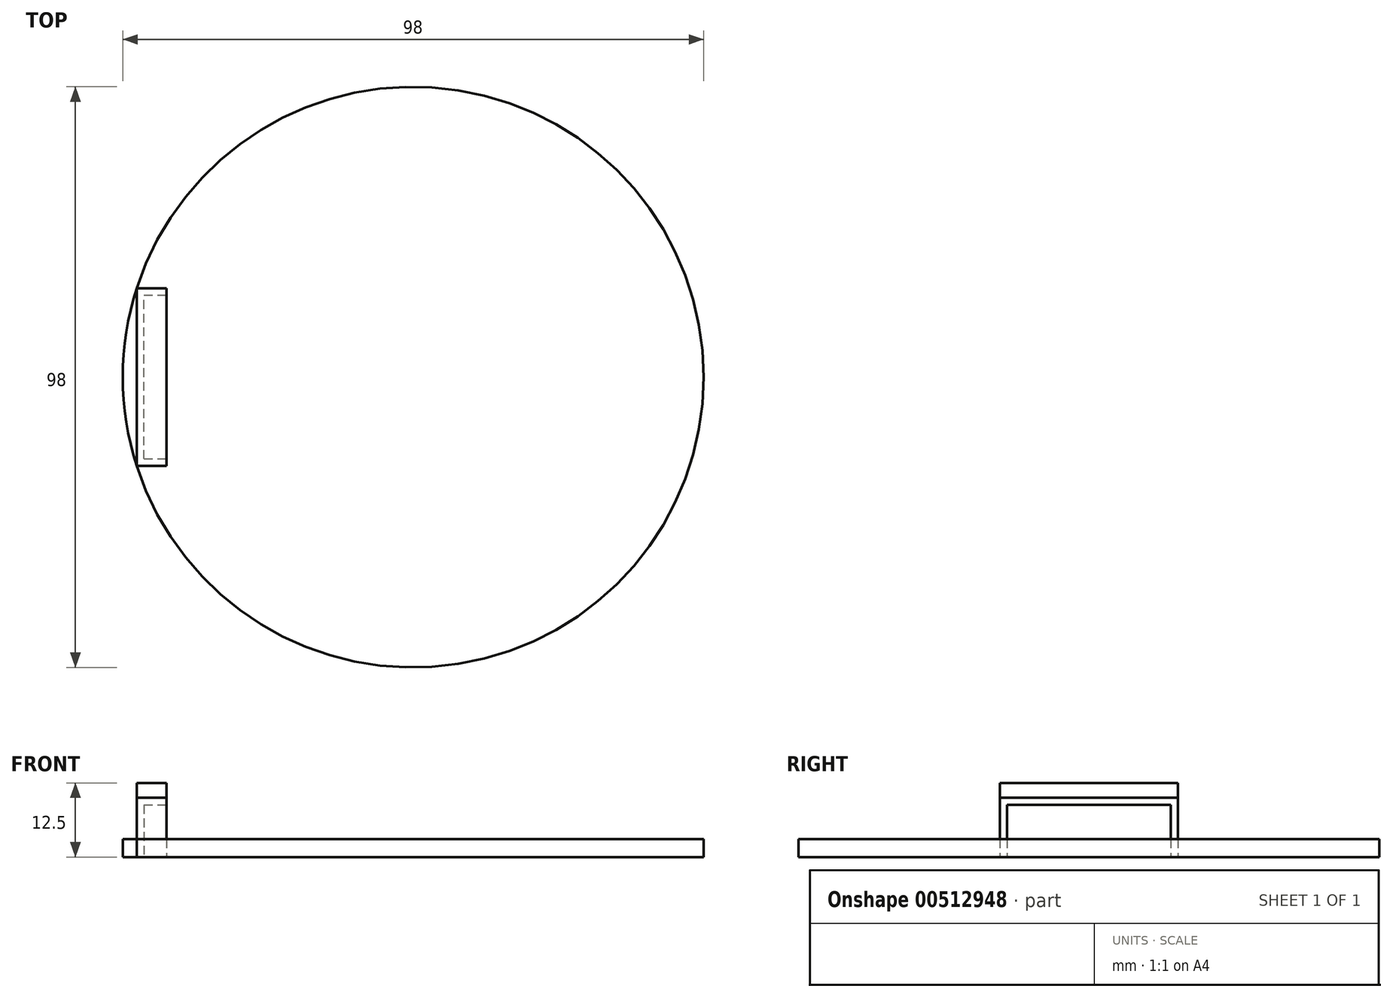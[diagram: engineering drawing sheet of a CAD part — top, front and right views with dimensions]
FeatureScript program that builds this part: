
annotation { "Feature Type Name" : "Feature", "Feature Type Description" : "" }
export const myFeature = defineFeature(function(context is Context, id is Id, definition is map)
    precondition{}
    {
        {
            var Q0;
            Q0=qCreatedBy(makeId("Top.planeOp"),FACE);
            var sketch = newSketch(context, id + "F0", { "sketchPlane" : qUnion([Q0])});
            skLineSegment(sketch, "E0", {"start": v(0, 0) * mm, "end": v(-49, 0) * mm});
            skArc(sketch, "E1", {"start": v(0, 49) * mm, "mid": v(-49, 0) * mm, "end": v(0, -49) * mm});
            skLineSegment(sketch, "E2", {"start": v(-46.65, -15) * mm, "end": v(-46.65, 15) * mm});
            skLineSegment(sketch, "E3", {"start": v(-46.65, -15) * mm, "end": v(-41.65, -15) * mm});
            skLineSegment(sketch, "E4", {"start": v(-41.65, -15) * mm, "end": v(-41.65, 15) * mm});
            skLineSegment(sketch, "E5", {"start": v(-41.65, 15) * mm, "end": v(-46.65, 15) * mm});
            skArc(sketch, "E6", {"start": v(0, -49) * mm, "mid": v(49, 0) * mm, "end": v(0, 49) * mm});
            skSolve(sketch);
        }
        {
            var Q0;
            {var subQ1=sQuery(id+"F0.wireOp",EDGE,"E3");Q0=makeQuery(id+"F0.imprint","IMPRINT",FACE,{"disambiguationData":[TD([[makeQuery(id+"F0.imprint","IMPRINT",EDGE,{"derivedFrom":subQ1}),-1.0]])]});}
            var Q1;
            {var subQ0=sQuery(id+"F0.wireOp",EDGE,"E1");var subQ1=sQuery(id+"F0.wireOp",EDGE,"E0");var subQ2=makeQuery(id+"F0.imprint","INTERSECT",VERTEX,{"derivedFrom":[subQ1,subQ0]});Q1=makeQuery(id+"F0.imprint","IMPRINT",FACE,{"disambiguationData":[TD([[makeQuery(id+"F0.imprint","IMPRINT",EDGE,{"disambiguationData":[TD([[subQ2,1.0]])],"derivedFrom":subQ1}),1.0]])]});}
            var Q2;
            {var subQ0=sQuery(id+"F0.wireOp",EDGE,"E1");var subQ1=sQuery(id+"F0.wireOp",EDGE,"E0");var subQ2=makeQuery(id+"F0.imprint","INTERSECT",VERTEX,{"derivedFrom":[subQ1,subQ0]});Q2=makeQuery(id+"F0.imprint","IMPRINT",FACE,{"disambiguationData":[TD([[makeQuery(id+"F0.imprint","IMPRINT",EDGE,{"disambiguationData":[TD([[subQ2,1.0]])],"derivedFrom":subQ1}),-1.0]])]});}
            extrude(context, id + "F1", {"entities" : qUnion([Q0, Q1, Q2]), "oppositeDirection" : true, "depth" : 3 * mm, "offsetDistance" : 25 * mm});
        }
        {
            var Q0;
            {var subQ5=sQuery(id+"F0.wireOp",EDGE,"E3");Q0=makeQuery(id+"F0.imprint","IMPRINT",FACE,{"disambiguationData":[TD([[makeQuery(id+"F0.imprint","IMPRINT",EDGE,{"derivedFrom":subQ5}),1.0]])]});}
            var Q1;
            {var subQ5=sQuery(id+"F0.wireOp",EDGE,"E5");Q1=makeQuery(id+"F0.imprint","IMPRINT",FACE,{"disambiguationData":[TD([[makeQuery(id+"F0.imprint","IMPRINT",EDGE,{"derivedFrom":subQ5}),1.0]])]});}
            var Q2;
            Q2=sQuery(id+"F0.wireOp",EDGE,"E3");
            var Q3;
            Q3=sQuery(id+"F0.wireOp",EDGE,"E2");
            var Q4;
            Q4=sQuery(id+"F0.wireOp",EDGE,"E5");
            extrude(context, id + "F2", {"entities" : qUnion([Q0, Q1]), "surfaceEntities" : qUnion([Q2, Q3, Q4]), "oppositeDirection" : true, "depth" : 10 * mm, "offsetDistance" : 25 * mm});
        }
        {
            var Q0;
            Q0=qCreatedBy(makeId("Top.planeOp"),FACE);
            cPlane(context, id + "F3", {"entities" : qUnion([Q0]), "cplaneType" : CPlaneType.OFFSET, "offset" : 10 * mm, "oppositeDirection" : true, "width" : 150 * mm, "height" : 150 * mm});
        }
        {
            var Q0;
            Q0=qCreatedBy(id+"F3.planeOp",FACE);
            var sketch = newSketch(context, id + "F4", { "sketchPlane" : qUnion([Q0])});
            skPoint(sketch, "E7.0", {"position": v(-41.65, 15) * mm});
            skPoint(sketch, "E8.0", {"position": v(-46.65, 15) * mm});
            skPoint(sketch, "E9.0", {"position": v(-46.65, -15) * mm});
            skPoint(sketch, "E10.0", {"position": v(-41.65, -15) * mm});
            skLineSegment(sketch, "E11", {"start": v(-46.65, 15) * mm, "end": v(-46.65, -15) * mm});
            skLineSegment(sketch, "E12", {"start": v(-41.65, -15) * mm, "end": v(-46.65, -15) * mm});
            skLineSegment(sketch, "E13", {"start": v(-46.65, 15) * mm, "end": v(-41.65, 15) * mm});
            skLineSegment(sketch, "E14", {"start": v(-41.65, 15) * mm, "end": v(-41.65, -15) * mm});
            skSolve(sketch);
        }
        {
            var Q0;
            Q0=qSketchRegion(id+"F4",true);
            var Q1;
            Q1=qConstructionFilter(qBodyType(qCreatedBy(id+"F4",EDGE),BodyType.WIRE),ConstructionObject.NO);
            extrude(context, id + "F5", {"entities" : qUnion([Q0]), "surfaceEntities" : qUnion([Q1]), "oppositeDirection" : true, "depth" : 2.5 * mm, "offsetDistance" : 25 * mm});
        }
        {
            var Q0;
            Q0=makeQuery(id+"F1.opExtrude","SWEPT_BODY",BODY,{"disambiguationData":[OSD([sQuery(id+"F0.wireOp",EDGE,"E1"),sQuery(id+"F0.wireOp",EDGE,"E3"),sQuery(id+"F0.wireOp",EDGE,"E4"),sQuery(id+"F0.wireOp",EDGE,"E5"),sQuery(id+"F0.wireOp",EDGE,"E6")])]});
            var Q1;
            Q1=makeQuery(id+"F1.opExtrude","SWEPT_BODY",BODY,{"disambiguationData":[OSD([sQuery(id+"F0.wireOp",EDGE,"E1"),sQuery(id+"F0.wireOp",EDGE,"E2")])]});
            var Q2;
            Q2=makeQuery(id+"F5.opExtrude","SWEPT_BODY",BODY,{"disambiguationData":[OSD([sQuery(id+"F4.wireOp",EDGE,"E11"),sQuery(id+"F4.wireOp",EDGE,"E12"),sQuery(id+"F4.wireOp",EDGE,"E13"),sQuery(id+"F4.wireOp",EDGE,"E14")])]});
            var Q3;
            Q3=makeQuery(id+"F2.opExtrude","SWEPT_BODY",BODY,{"disambiguationData":[OSD([sQuery(id+"F0.wireOp",EDGE,"E5")])]});
            var Q4;
            Q4=qCreatedBy(makeId("Top.planeOp"),FACE);
            mirror(context, id + "F6", {"entities" : qUnion([Q0, Q1, Q2, Q3]), "mirrorPlane" : qUnion([Q4])});
        }
        {
            var Q0;
            Q0=makeQuery(id+"F1.opExtrude","SWEPT_BODY",BODY,{"disambiguationData":[OSD([sQuery(id+"F0.wireOp",EDGE,"E1"),sQuery(id+"F0.wireOp",EDGE,"E3"),sQuery(id+"F0.wireOp",EDGE,"E4"),sQuery(id+"F0.wireOp",EDGE,"E5"),sQuery(id+"F0.wireOp",EDGE,"E6")])]});
            var Q1;
            Q1=makeQuery(id+"F1.opExtrude","SWEPT_BODY",BODY,{"disambiguationData":[OSD([sQuery(id+"F0.wireOp",EDGE,"E1"),sQuery(id+"F0.wireOp",EDGE,"E2")])]});
            var Q2;
            Q2=makeQuery(id+"F5.opExtrude","SWEPT_BODY",BODY,{"disambiguationData":[OSD([sQuery(id+"F4.wireOp",EDGE,"E11"),sQuery(id+"F4.wireOp",EDGE,"E12"),sQuery(id+"F4.wireOp",EDGE,"E13"),sQuery(id+"F4.wireOp",EDGE,"E14")])]});
            deleteBodies(context, id + "F7", {"entities" : qUnion([Q0, Q1, Q2])});
        }
        {
            var Q0;
            Q0=makeQuery(id+"F2.opExtrude","SWEPT_BODY",BODY,{"disambiguationData":[OSD([sQuery(id+"F0.wireOp",EDGE,"E5")])]});
            deleteBodies(context, id + "F8", {"entities" : qUnion([Q0])});
        }
        {
            var Q0;
            Q0=makeQuery(id+"F6.opPattern","COPY",FACE,{"derivedFrom":makeQuery(id+"F2.opExtrude","SWEPT_FACE",FACE,{"disambiguationData":[OSD([sQuery(id+"F0.wireOp",EDGE,"E4")])]}),"instanceName":"1"});
            var Q1;
            Q1=makeQuery(id+"F6.opPattern","COPY",FACE,{"derivedFrom":makeQuery(id+"F2.opExtrude","CAP_FACE",FACE,{"disambiguationData":[OSD([sQuery(id+"F0.wireOp",EDGE,"E2"),sQuery(id+"F0.wireOp",EDGE,"E3"),sQuery(id+"F0.wireOp",EDGE,"E4"),sQuery(id+"F0.wireOp",EDGE,"E5")])],"isStart":true}),"instanceName":"1"});
            shell(context, id + "F9", {"entities" : qUnion([Q0, Q1]), "thickness" : 1.2 * mm});
        }
    });
